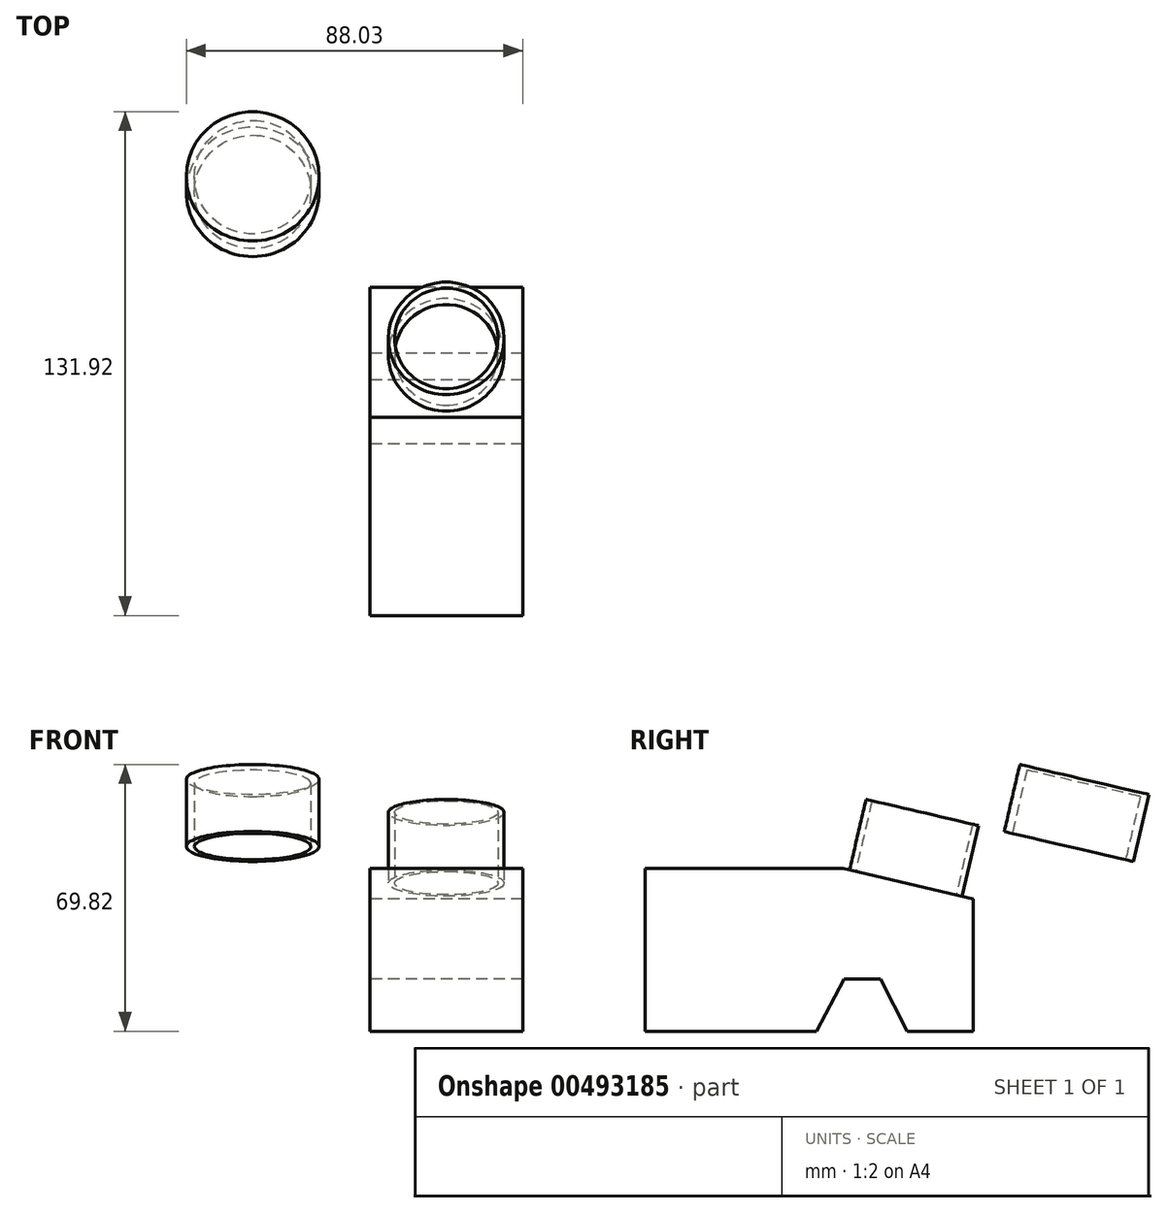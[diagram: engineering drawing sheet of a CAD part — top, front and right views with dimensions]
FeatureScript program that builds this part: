
annotation { "Feature Type Name" : "Feature", "Feature Type Description" : "" }
export const myFeature = defineFeature(function(context is Context, id is Id, definition is map)
    precondition{}
    {
        {
            var Q0;
            Q0=qCreatedBy(makeId("Right.planeOp"),FACE);
            var sketch = newSketch(context, id + "F0", { "sketchPlane" : qUnion([Q0])});
            skLineSegment(sketch, "E0", {"start": v(-63.62, -18.73) * mm, "end": v(-18.73, -18.73) * mm});
            skLineSegment(sketch, "E1", {"start": v(-18.73, -18.73) * mm, "end": v(-11.52, -5.04) * mm});
            skLineSegment(sketch, "E2", {"start": v(-11.52, -5.04) * mm, "end": v(-1.92, -5.04) * mm});
            skLineSegment(sketch, "E3", {"start": v(-1.92, -5.04) * mm, "end": v(5.04, -18.73) * mm});
            skLineSegment(sketch, "E4", {"start": v(5.04, -18.73) * mm, "end": v(22.33, -18.73) * mm});
            skLineSegment(sketch, "E5", {"start": v(22.33, -18.73) * mm, "end": v(22.33, 15.93) * mm});
            skLineSegment(sketch, "E6", {"start": v(22.33, 15.93) * mm, "end": v(-11.76, 23.85) * mm});
            skLineSegment(sketch, "E7", {"start": v(-11.76, 23.85) * mm, "end": v(-63.62, 23.85) * mm});
            skLineSegment(sketch, "E8", {"start": v(-63.62, 23.85) * mm, "end": v(-63.62, -18.73) * mm});
            skSolve(sketch);
        }
        {
            var Q0;
            Q0=makeQuery(id+"F0.imprint","IMPRINT",FACE,{"disambiguationData":[TD([[makeQuery(id+"F0.imprint","IMPRINT",EDGE,{"derivedFrom":sQuery(id+"F0.wireOp",EDGE,"E0")}),1.0]])]});
            extrude(context, id + "F1", {"entities" : qUnion([Q0]), "endBound" : BoundingType.SYMMETRIC, "depth" : 40 * mm});
        }
        {
            var Q0;
            Q0=makeQuery(id+"F1.opExtrude","SWEPT_FACE",FACE,{"disambiguationData":[OSD([sQuery(id+"F0.wireOp",EDGE,"E6")])]});
            var sketch = newSketch(context, id + "F2", { "sketchPlane" : qUnion([Q0])});
            skCircle(sketch, "E9", {"center": v(0, 0) * mm, "radius": 15.13 * mm});
            skCircle(sketch, "E10", {"center": v(0, 0) * mm, "radius": 13.52 * mm});
            skSolve(sketch);
        }
        {
            var Q0;
            Q0=makeQuery(id+"F2.imprint","IMPRINT",FACE,{"disambiguationData":[TD([[makeQuery(id+"F2.imprint","IMPRINT",EDGE,{"derivedFrom":sQuery(id+"F2.wireOp",EDGE,"E9")}),1.0]])]});
            extrude(context, id + "F3", {"entities" : qUnion([Q0]), "operationType" : NewBodyOperationType.ADD, "depth" : 19 * mm});
        }
        {
            var Q0;
            Q0=makeQuery(id+"F3.opExtrude","CAP_FACE",FACE,{"disambiguationData":[OSD([sQuery(id+"F2.wireOp",EDGE,"E9"),sQuery(id+"F2.wireOp",EDGE,"E10")])],"isStart":false});
            var sketch = newSketch(context, id + "F4", { "sketchPlane" : qUnion([Q0])});
            skCircle(sketch, "E11", {"center": v(-50.66, 39.38) * mm, "radius": 17.37 * mm});
            skSolve(sketch);
        }
        {
            var Q0;
            Q0=makeQuery(id+"F4.imprint","IMPRINT",FACE,{"disambiguationData":[TD([[makeQuery(id+"F4.imprint","IMPRINT",EDGE,{"derivedFrom":sQuery(id+"F4.wireOp",EDGE,"E11")}),1.0]])]});
            extrude(context, id + "F5", {"entities" : qUnion([Q0]), "depth" : 18 * mm});
        }
        {
            var Q0;
            Q0=makeQuery(id+"F5.opExtrude","CAP_FACE",FACE,{"disambiguationData":[OSD([sQuery(id+"F4.wireOp",EDGE,"E11")])],"isStart":true});
            var sketch = newSketch(context, id + "F6", { "sketchPlane" : qUnion([Q0])});
            skCircle(sketch, "E12", {"center": v(-50.66, -39.38) * mm, "radius": 15.25 * mm});
            skSolve(sketch);
        }
        {
            var Q0;
            Q0=makeQuery(id+"F6.imprint","IMPRINT",FACE,{"disambiguationData":[TD([[makeQuery(id+"F6.imprint","IMPRINT",EDGE,{"derivedFrom":sQuery(id+"F6.wireOp",EDGE,"E12")}),1.0]])]});
            extrude(context, id + "F7", {"entities" : qUnion([Q0]), "operationType" : NewBodyOperationType.REMOVE, "oppositeDirection" : true, "depth" : 17 * mm});
        }
    });
